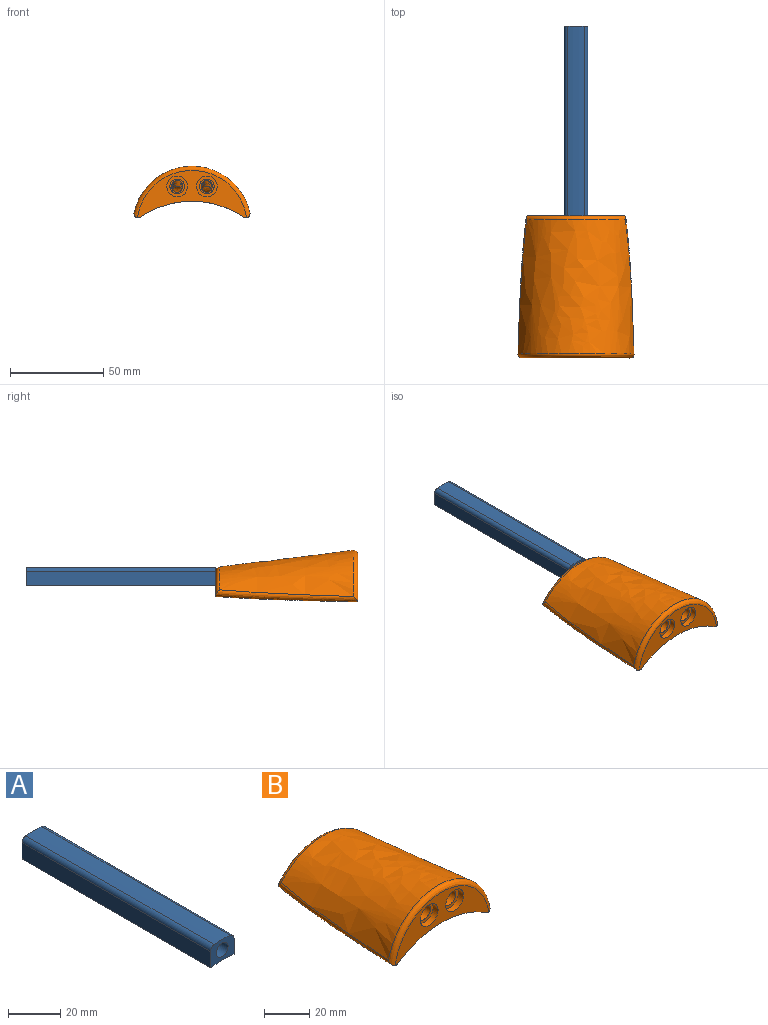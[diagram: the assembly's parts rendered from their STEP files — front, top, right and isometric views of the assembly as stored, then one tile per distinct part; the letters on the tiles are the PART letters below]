
ASSEMBLY  parts=2 mates=1
PART A: 9 faces, bbox 12.7x101.6x10.1 mm
  f0: cylinder r=48.9mm len=101.6mm, axis (0,1,0), area 1294mm2, adj f1,f3,f5,f6
  f1: plane 101.6x7.57mm, normal (1,0,0), area 769.4mm2, adj f0,f5,f6,f7
  f2: cylinder r=34.34mm len=101.6mm, axis (0,1,0), area 887.1mm2, adj f5,f6,f7,f8
  f3: plane 101.6x7.57mm, normal (-1,0,0), area 769.4mm2, adj f0,f5,f6,f8
  f4: cylinder r=3.17mm len=101.6mm, axis (0,1,0), area 2026.8mm2, adj f5,f6
  f5: plane 12.7x10.12mm, normal (0,-1,0), area 89.2mm2, adj f0,f1,f2,f3,f4,f7,f8
  f6: plane 12.7x10.12mm, normal (0,1,0), area 89.2mm2, adj f0,f1,f2,f3,f4,f7,f8
  f7: cylinder r=2.29mm len=101.6mm, axis (0,1,0), area 335.3mm2, adj f1,f2,f5,f6
  f8: cylinder r=2.29mm len=101.6mm, axis (0,1,0), area 335.3mm2, adj f2,f3,f5,f6
PART B: 22 faces, bbox 71.9x94.8x34.5 mm
  f0: plane 58.55x25.5mm, normal (0,-1,0), area 589.1mm2, adj f1,f17,f18,f19,f20,f21
  f1: bspline ~91.13x11.55mm, area 440.7mm2, adj f0,f2,f3,f16,f17,f19
  f2: plane 51.85x13.92mm, normal (0,1,0), area 273.2mm2, adj f1,f3,f18,f19
  f3: bspline ~57.85x17.93mm, area 202.1mm2, adj f1,f2,f4,f10,f16,f18
  f4: bspline ~25.2x13.07mm, area 345.6mm2, adj f3,f5,f6,f10
  f5: plane 5.86x3.18mm, normal (0,-1,0), area 15.3mm2, adj f4
  f6: bspline ~28.97x11.92mm, area 366.2mm2, adj f4,f7
  f7: plane 11.47x11.47mm, normal (0,-1,0), area 18.8mm2, adj f6,f8
  f8: cylinder r=3.92mm len=34.93mm, axis (0,-1,0), area 861.1mm2, adj f7,f9
  f9: plane 11.11x11.11mm, normal (0,-1,0), area 48.6mm2, adj f8,f21
  f10: bspline ~19.29x14.33mm, area 350.6mm2, adj f3,f4,f11,f12
  f11: plane 7.08x4.39mm, normal (0,-1,0), area -3.3mm2, adj f10
  f12: bspline ~31.39x11.92mm, area 366.2mm2, adj f10,f13
  f13: plane 11.42x11.42mm, normal (0,-1,0), area 18.8mm2, adj f12,f14
  f14: cylinder r=3.92mm len=34.93mm, axis (0,-1,0), area 861.1mm2, adj f13,f15
  f15: plane 11.11x11.11mm, normal (0,-1,0), area 48.6mm2, adj f14,f20
  f16: bspline ~76.2x63.5mm, area 5211mm2, adj f1,f3,f17,f18
  f17: bspline ~63.46x30.5mm, area 326.1mm2, adj f0,f1,f16,f18
  f18: bspline ~90.18x11.42mm, area 440.7mm2, adj f0,f2,f3,f16,f17,f19
  f19: cylinder r=48.9mm len=76.2mm, axis (0,-1,0), area 4065.7mm2, adj f0,f1,f2,f18
  f20: cylinder r=5.56mm len=11.11mm, axis (0,-1,0), area 110.8mm2, adj f0,f15
  f21: cylinder r=5.56mm len=11.11mm, axis (0,-1,0), area 110.8mm2, adj f0,f9
PLACE A rot(axis=(0,0,1),180deg) t=(18.78,268.75,16.14)mm
PLACE B t=(18.78,192.55,16.14)mm
MATE fastened B.f19 <-> A.f0  axis (0,1,0) through (18.78,268.75,16.14)mm
